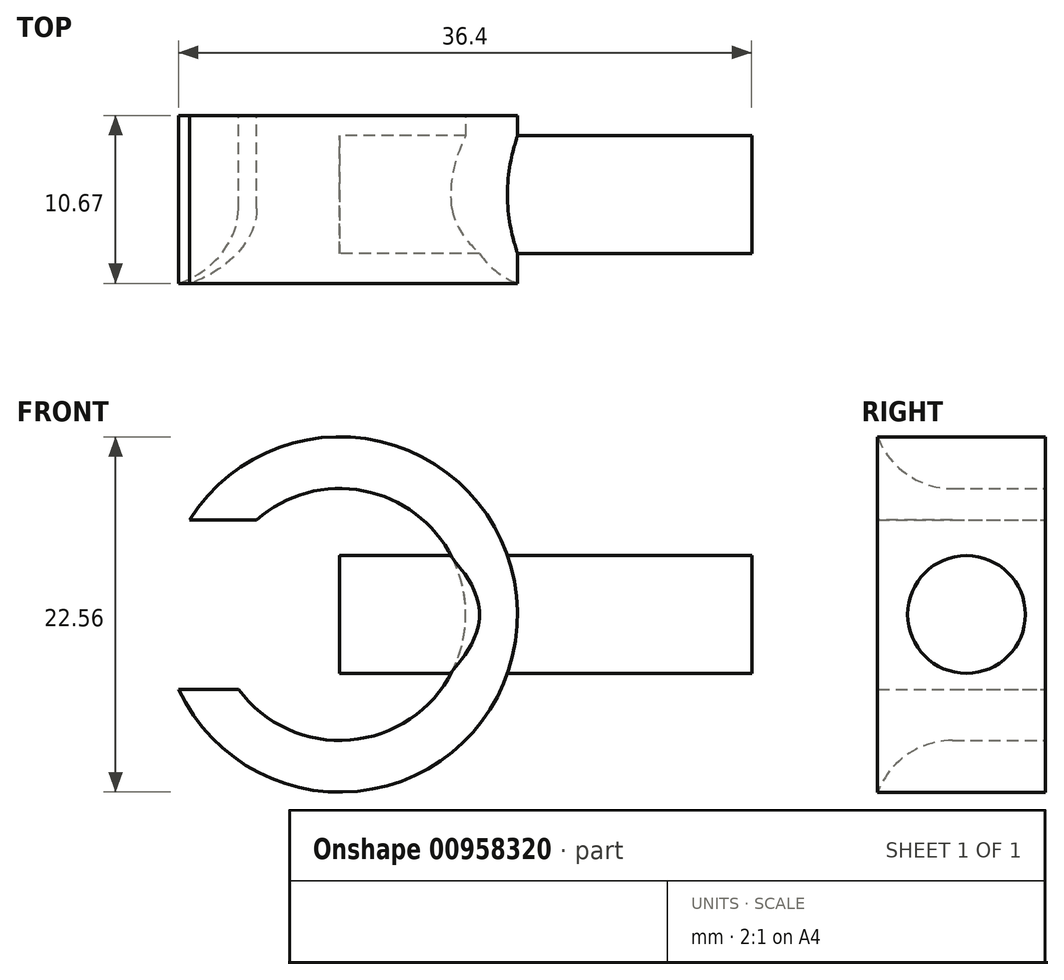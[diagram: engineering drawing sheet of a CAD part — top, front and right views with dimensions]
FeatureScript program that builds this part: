
annotation { "Feature Type Name" : "Feature", "Feature Type Description" : "" }
export const myFeature = defineFeature(function(context is Context, id is Id, definition is map)
    precondition{}
    {
        {
            var Q0;
            Q0=qCreatedBy(makeId("Front.planeOp"),FACE);
            var sketch = newSketch(context, id + "F0", { "sketchPlane" : qUnion([Q0])});
            skCircle(sketch, "E0", {"center": v(0, 0) * mm, "radius": 11.28 * mm});
            skSolve(sketch);
        }
        {
            var Q0;
            Q0 = qSketchRegion(id + "F0", true);
            extrude(context, id + "F1", {"entities" : qUnion([Q0]), "depth" : 10.67 * mm, "offsetDistance" : 25.4 * mm});
        }
        {
            var Q0;
            Q0=qCreatedBy(makeId("Front.planeOp"),FACE);
            var sketch = newSketch(context, id + "F2", { "sketchPlane" : qUnion([Q0])});
            skCircle(sketch, "E1", {"center": v(0, 0) * mm, "radius": 8 * mm});
            skSolve(sketch);
        }
        {
            var Q0;
            Q0 = qSketchRegion(id + "F2", true);
            extrude(context, id + "F3", {"entities" : qUnion([Q0]), "operationType" : NewBodyOperationType.REMOVE, "depth" : 30.73 * mm, "offsetDistance" : 25.4 * mm});
        }
        {
            var Q0;
            Q0=qCreatedBy(makeId("Front.planeOp"),FACE);
            var sketch = newSketch(context, id + "F4", { "sketchPlane" : qUnion([Q0])});
            skLineSegment(sketch, "E2.bottom", {"start": v(-15.5, 0) * mm, "end": v(-4.46, 0) * mm});
            skLineSegment(sketch, "E2.top", {"start": v(-15.5, 6.02) * mm, "end": v(-4.46, 6.02) * mm});
            skLineSegment(sketch, "E2.left", {"start": v(-15.5, 0) * mm, "end": v(-15.5, 6.02) * mm});
            skLineSegment(sketch, "E2.right", {"start": v(-4.46, 0) * mm, "end": v(-4.46, 6.02) * mm});
            skLineSegment(sketch, "E3.bottom", {"start": v(-15.5, 0) * mm, "end": v(-4.32, 0) * mm});
            skLineSegment(sketch, "E3.top", {"start": v(-15.5, -4.74) * mm, "end": v(-4.32, -4.74) * mm});
            skLineSegment(sketch, "E3.left", {"start": v(-15.5, 0) * mm, "end": v(-15.5, -4.74) * mm});
            skLineSegment(sketch, "E3.right", {"start": v(-4.32, 0) * mm, "end": v(-4.32, -4.74) * mm});
            skSolve(sketch);
        }
        {
            var Q0;
            Q0 = qSketchRegion(id + "F4", true);
            extrude(context, id + "F5", {"entities" : qUnion([Q0]), "operationType" : NewBodyOperationType.REMOVE, "depth" : 41.4 * mm, "offsetDistance" : 25.4 * mm});
        }
        {
            var Q0;
            Q0=qCreatedBy(makeId("Right.planeOp"),FACE);
            var sketch = newSketch(context, id + "F6", { "sketchPlane" : qUnion([Q0])});
            skCircle(sketch, "E4", {"center": v(-5.03, 0) * mm, "radius": 3.74 * mm});
            skSolve(sketch);
        }
        {
            var Q0;
            Q0=makeQuery(id+"F6.imprint","IMPRINT",FACE,{"disambiguationData":[TD([[makeQuery(id+"F6.imprint","IMPRINT",EDGE,{"derivedFrom":sQuery(id+"F6.wireOp",EDGE,"E4")}),1.0]])]});
            extrude(context, id + "F7", {"entities" : qUnion([Q0]), "operationType" : NewBodyOperationType.ADD, "depth" : 26.16 * mm, "offsetDistance" : 25.4 * mm});
        }
        {
            var Q0;
            Q0=makeQuery(id+"F3.boolean.opBoolean","COPY",EDGE,{"derivedFrom":makeQuery(id+"F3.opExtrude","CAP_EDGE",EDGE,{"disambiguationData":[OSD([sQuery(id+"F2.wireOp",EDGE,"E1")])],"isStart":true})});
            var Q1;
            Q1=makeQuery(id+"F3.boolean.opBoolean","INTERSECT",EDGE,{"derivedFrom":[makeQuery(id+"F1.opExtrude","CAP_FACE",FACE,{"disambiguationData":[OSD([sQuery(id+"F0.wireOp",EDGE,"E0")])],"isStart":false}),makeQuery(id+"F3.opExtrude","SWEPT_FACE",FACE,{"disambiguationData":[OSD([sQuery(id+"F2.wireOp",EDGE,"E1")])]})]});
            fillet(context, id + "F8", {"entities" : qUnion([Q0, Q1]), "radius" : 5.08 * mm, "tangentPropagation" : true, "allowEdgeOverflow" : false});
        }
    });
